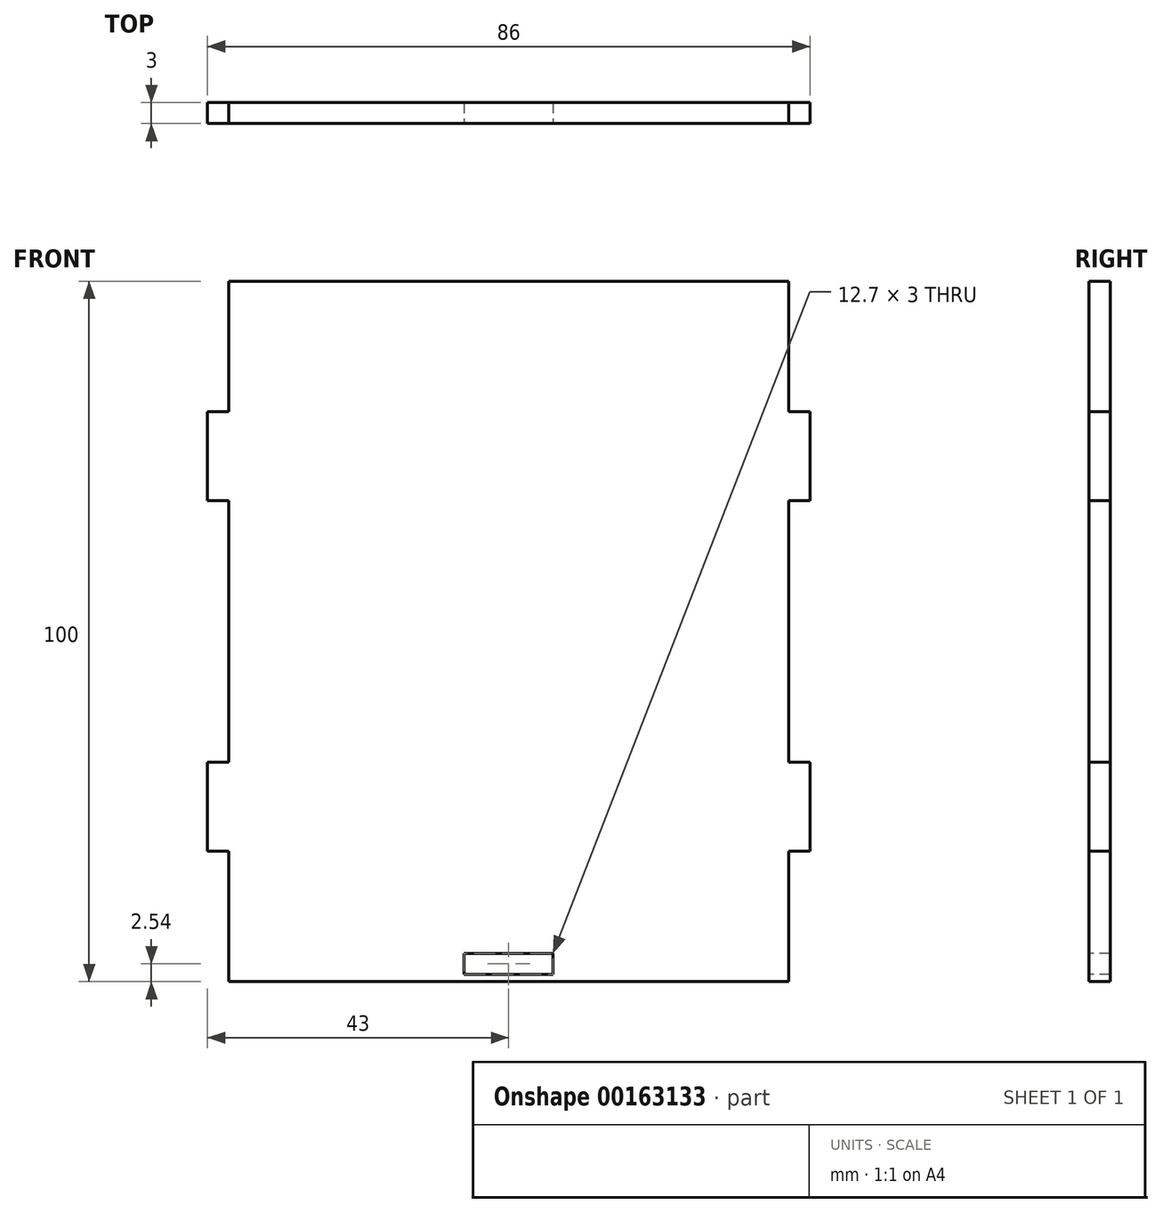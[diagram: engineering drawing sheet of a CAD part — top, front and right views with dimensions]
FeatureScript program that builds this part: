
annotation { "Feature Type Name" : "Feature", "Feature Type Description" : "" }
export const myFeature = defineFeature(function(context is Context, id is Id, definition is map)
    precondition{}
    {
        {
            var Q0;
            Q0=qCreatedBy(makeId("Front.planeOp"),FACE);
            var sketch = newSketch(context, id + "F0", { "sketchPlane" : qUnion([Q0])});
            skLineSegment(sketch, "E0.bottom", {"start": v(-40, 50) * mm, "end": v(40, 50) * mm});
            skLineSegment(sketch, "E0.top", {"start": v(-40, -50) * mm, "end": v(40, -50) * mm});
            skLineSegment(sketch, "E0.left", {"start": v(-40, 50) * mm, "end": v(-40, 31.35) * mm});
            skLineSegment(sketch, "E0.right", {"start": v(40, 50) * mm, "end": v(40, 31.35) * mm});
            skPoint(sketch, "E0.middle", {"position": v(0, 0) * mm});
            skLineSegment(sketch, "E1.bottom", {"start": v(-43, 31.35) * mm, "end": v(-40, 31.35) * mm});
            skLineSegment(sketch, "E1.top", {"start": v(-43, 18.65) * mm, "end": v(-40, 18.65) * mm});
            skLineSegment(sketch, "E1.left", {"start": v(-43, 31.35) * mm, "end": v(-43, 18.65) * mm});
            skLineSegment(sketch, "E2.trimOffspring", {"start": v(-40, 18.65) * mm, "end": v(-40, -18.65) * mm});
            skLineSegment(sketch, "E3", {"start": v(40, 31.35) * mm, "end": v(43, 31.35) * mm});
            skLineSegment(sketch, "E4", {"start": v(43, 31.35) * mm, "end": v(43, 18.65) * mm});
            skLineSegment(sketch, "E5", {"start": v(43, 18.65) * mm, "end": v(40, 18.65) * mm});
            skLineSegment(sketch, "E6.trimOffspring", {"start": v(40, 18.65) * mm, "end": v(40, -18.65) * mm});
            skLineSegment(sketch, "E7", {"start": v(-40, -18.65) * mm, "end": v(-43, -18.65) * mm});
            skLineSegment(sketch, "E8", {"start": v(-43, -18.65) * mm, "end": v(-43, -31.35) * mm});
            skLineSegment(sketch, "E9", {"start": v(-43, -31.35) * mm, "end": v(-40, -31.35) * mm});
            skLineSegment(sketch, "E10.trimOffspring", {"start": v(-40, -31.35) * mm, "end": v(-40, -50) * mm});
            skLineSegment(sketch, "E11", {"start": v(40, -18.65) * mm, "end": v(43, -18.65) * mm});
            skLineSegment(sketch, "E12", {"start": v(43, -18.65) * mm, "end": v(43, -31.35) * mm});
            skLineSegment(sketch, "E13", {"start": v(43, -31.35) * mm, "end": v(40, -31.35) * mm});
            skLineSegment(sketch, "E14.trimOffspring", {"start": v(40, -31.35) * mm, "end": v(40, -50) * mm});
            skLineSegment(sketch, "E15", {"start": v(-43, 25) * mm, "end": v(43, 25) * mm, "construction": true});
            skPoint(sketch, "E16.endSnap0", {"position": v(43, -25) * mm});
            skLineSegment(sketch, "E17", {"start": v(-43, -25) * mm, "end": v(43, -25) * mm, "construction": true});
            skSolve(sketch);
        }
        {
            var Q0;
            Q0 = qSketchRegion(id + "F0", true);
            extrude(context, id + "F1", {"entities" : qUnion([Q0]), "depth" : 3 * mm});
        }
        {
            var Q0;
            Q0=makeQuery(id+"F1.opExtrude","CAP_FACE",FACE,{"disambiguationData":[OSD([sQuery(id+"F0.wireOp",EDGE,"E0.bottom"),sQuery(id+"F0.wireOp",EDGE,"E0.top"),sQuery(id+"F0.wireOp",EDGE,"E0.left"),sQuery(id+"F0.wireOp",EDGE,"E0.right"),sQuery(id+"F0.wireOp",EDGE,"E1.bottom"),sQuery(id+"F0.wireOp",EDGE,"E1.top"),sQuery(id+"F0.wireOp",EDGE,"E1.left"),sQuery(id+"F0.wireOp",EDGE,"E2.trimOffspring"),sQuery(id+"F0.wireOp",EDGE,"E3"),sQuery(id+"F0.wireOp",EDGE,"E4"),sQuery(id+"F0.wireOp",EDGE,"E5"),sQuery(id+"F0.wireOp",EDGE,"E6.trimOffspring"),sQuery(id+"F0.wireOp",EDGE,"E7"),sQuery(id+"F0.wireOp",EDGE,"E8"),sQuery(id+"F0.wireOp",EDGE,"E9"),sQuery(id+"F0.wireOp",EDGE,"E10.trimOffspring"),sQuery(id+"F0.wireOp",EDGE,"E11"),sQuery(id+"F0.wireOp",EDGE,"E12"),sQuery(id+"F0.wireOp",EDGE,"E13"),sQuery(id+"F0.wireOp",EDGE,"E14.trimOffspring")])],"isStart":false});
            var sketch = newSketch(context, id + "F2", { "sketchPlane" : qUnion([Q0])});
            skLineSegment(sketch, "E18.bottom", {"start": v(-6.35, -45.96) * mm, "end": v(6.35, -45.96) * mm});
            skLineSegment(sketch, "E18.top", {"start": v(-6.35, -48.96) * mm, "end": v(6.35, -48.96) * mm});
            skLineSegment(sketch, "E18.left", {"start": v(-6.35, -45.96) * mm, "end": v(-6.35, -48.96) * mm});
            skLineSegment(sketch, "E18.right", {"start": v(6.35, -45.96) * mm, "end": v(6.35, -48.96) * mm});
            skPoint(sketch, "E18.middle", {"position": v(0, -47.46) * mm});
            skSolve(sketch);
        }
        {
            var Q0;
            Q0 = qSketchRegion(id + "F2", true);
            extrude(context, id + "F3", {"entities" : qUnion([Q0]), "operationType" : NewBodyOperationType.REMOVE, "endBound" : BoundingType.UP_TO_NEXT, "oppositeDirection" : true, "depth" : 25.4 * mm});
        }
    });
